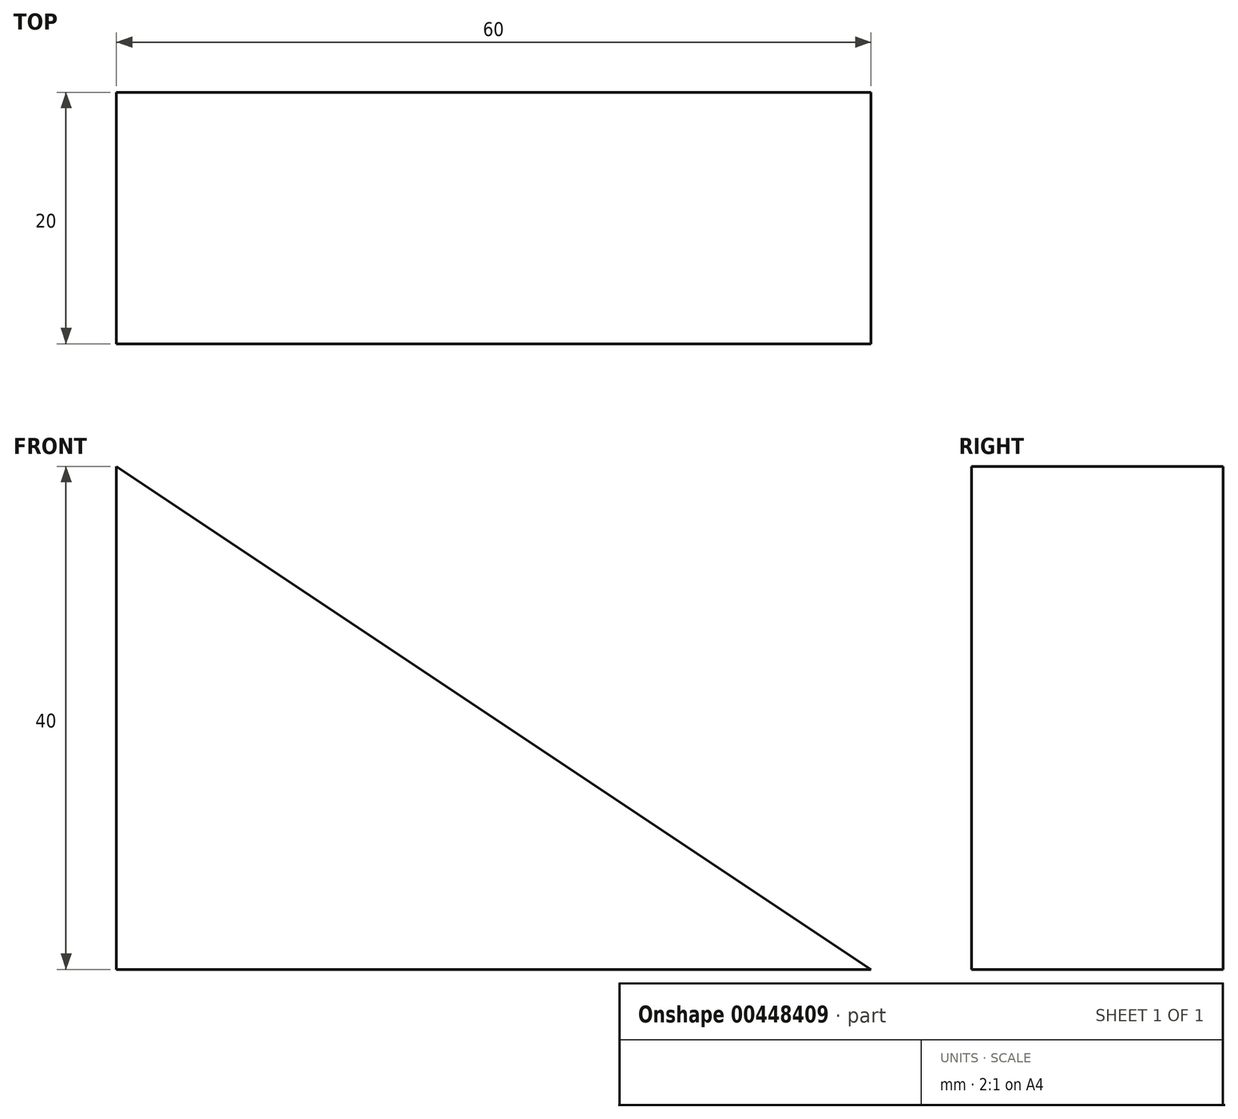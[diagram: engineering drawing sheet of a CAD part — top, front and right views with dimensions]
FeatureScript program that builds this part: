
annotation { "Feature Type Name" : "Feature", "Feature Type Description" : "" }
export const myFeature = defineFeature(function(context is Context, id is Id, definition is map)
    precondition{}
    {
        {
            var Q0;
            Q0=qCreatedBy(makeId("Front.planeOp"),FACE);
            var sketch = newSketch(context, id + "F0", { "sketchPlane" : qUnion([Q0])});
            skLineSegment(sketch, "E0", {"start": v(0, 0) * mm, "end": v(60, 0) * mm});
            skLineSegment(sketch, "E1", {"start": v(60, 0) * mm, "end": v(0, 40) * mm});
            skLineSegment(sketch, "E2", {"start": v(0, 40) * mm, "end": v(0, 0) * mm});
            skSolve(sketch);
        }
        {
            var Q0;
            Q0=makeQuery(id+"F0.imprint","IMPRINT",FACE,{"disambiguationData":[TD([[makeQuery(id+"F0.imprint","IMPRINT",EDGE,{"derivedFrom":sQuery(id+"F0.wireOp",EDGE,"E0")}),1.0]])]});
            extrude(context, id + "F1", {"entities" : qUnion([Q0]), "depth" : 20 * mm});
        }
    });
